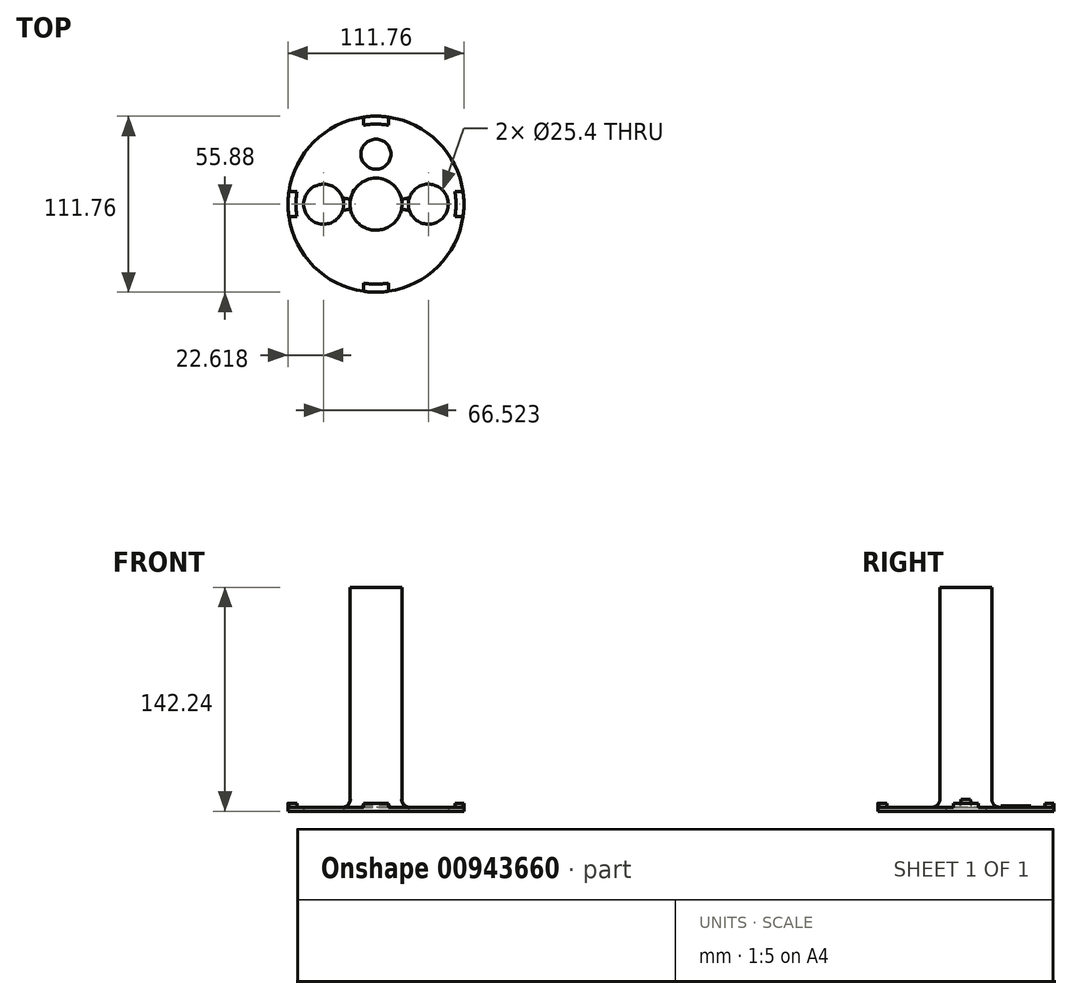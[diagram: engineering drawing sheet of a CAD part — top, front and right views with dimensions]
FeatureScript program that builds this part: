
annotation { "Feature Type Name" : "Feature", "Feature Type Description" : "" }
export const myFeature = defineFeature(function(context is Context, id is Id, definition is map)
    precondition{}
    {
        {
            var Q0;
            Q0=qCreatedBy(makeId("Top.planeOp"),FACE);
            var sketch = newSketch(context, id + "F0", { "sketchPlane" : qUnion([Q0])});
            skCircle(sketch, "E0", {"center": v(0, 0) * mm, "radius": 55.88 * mm});
            skCircle(sketch, "E1", {"center": v(0, 0) * mm, "radius": 16.51 * mm});
            skCircle(sketch, "E2", {"center": v(-33.26, 0) * mm, "radius": 12.7 * mm});
            skCircle(sketch, "E3.MirrorC", {"center": v(33.26, 0) * mm, "radius": 12.7 * mm});
            skCircle(sketch, "E4", {"center": v(0, 0) * mm, "radius": 50.8 * mm});
            skLineSegment(sketch, "E5", {"start": v(-50.18, 7.91) * mm, "end": v(-55.32, 7.91) * mm});
            skLineSegment(sketch, "E6.MirrorCS", {"start": v(-50.18, -7.91) * mm, "end": v(-55.32, -7.91) * mm});
            skLineSegment(sketch, "E7.1.0", {"start": v(-7.91, -50.18) * mm, "end": v(-7.91, -55.32) * mm});
            skLineSegment(sketch, "E7.1.1", {"start": v(7.91, -50.18) * mm, "end": v(7.91, -55.32) * mm});
            skLineSegment(sketch, "E7.2.0", {"start": v(50.18, -7.91) * mm, "end": v(55.32, -7.91) * mm});
            skLineSegment(sketch, "E7.2.1", {"start": v(50.18, 7.91) * mm, "end": v(55.32, 7.91) * mm});
            skLineSegment(sketch, "E7.3.0", {"start": v(7.91, 50.18) * mm, "end": v(7.91, 55.32) * mm});
            skLineSegment(sketch, "E7.3.1", {"start": v(-7.91, 50.18) * mm, "end": v(-7.91, 55.32) * mm});
            skSolve(sketch);
        }
        {
            var Q0;
            Q0 = qSketchRegion(id + "F0", true);
            var Q1;
            Q1=makeQuery(id+"F0.imprint","IMPRINT",FACE,{"disambiguationData":[TD([[makeQuery(id+"F0.imprint","IMPRINT",EDGE,{"derivedFrom":sQuery(id+"F0.wireOp",EDGE,"E1")}),-1.0]])]});
            var Q2;
            Q2=makeQuery(id+"F0.imprint","IMPRINT",FACE,{"disambiguationData":[TD([[makeQuery(id+"F0.imprint","IMPRINT",EDGE,{"derivedFrom":sQuery(id+"F0.wireOp",EDGE,"E1")}),1.0]])]});
            extrude(context, id + "F1", {"entities" : qUnion([Q0, Q1, Q2]), "depth" : 2.54 * mm, "offsetDistance" : 25.4 * mm});
        }
        {
            var Q0;
            {var subQ0=sQuery(id+"F0.wireOp",EDGE,"E5");Q0=makeQuery(id+"F0.imprint","IMPRINT",FACE,{"disambiguationData":[TD([[makeQuery(id+"F0.imprint","IMPRINT",EDGE,{"derivedFrom":subQ0}),1.0]])]});}
            var Q1;
            {var subQ0=sQuery(id+"F0.wireOp",EDGE,"E7.3.0");Q1=makeQuery(id+"F0.imprint","IMPRINT",FACE,{"disambiguationData":[TD([[makeQuery(id+"F0.imprint","IMPRINT",EDGE,{"derivedFrom":subQ0}),1.0]])]});}
            var Q2;
            {var subQ0=sQuery(id+"F0.wireOp",EDGE,"E7.2.0");Q2=makeQuery(id+"F0.imprint","IMPRINT",FACE,{"disambiguationData":[TD([[makeQuery(id+"F0.imprint","IMPRINT",EDGE,{"derivedFrom":subQ0}),1.0]])]});}
            var Q3;
            {var subQ0=sQuery(id+"F0.wireOp",EDGE,"E7.1.0");Q3=makeQuery(id+"F0.imprint","IMPRINT",FACE,{"disambiguationData":[TD([[makeQuery(id+"F0.imprint","IMPRINT",EDGE,{"derivedFrom":subQ0}),1.0]])]});}
            extrude(context, id + "F2", {"entities" : qUnion([Q0, Q1, Q2, Q3]), "operationType" : NewBodyOperationType.ADD, "depth" : 5.08 * mm, "offsetDistance" : 25.4 * mm});
        }
        {
            var Q0;
            Q0=makeQuery(id+"F0.imprint","IMPRINT",FACE,{"disambiguationData":[TD([[makeQuery(id+"F0.imprint","IMPRINT",EDGE,{"derivedFrom":sQuery(id+"F0.wireOp",EDGE,"E1")}),1.0]])]});
            extrude(context, id + "F3", {"entities" : qUnion([Q0]), "operationType" : NewBodyOperationType.ADD, "depth" : 142.24 * mm, "offsetDistance" : 25.4 * mm});
        }
        {
            var Q0;
            Q0=makeQuery(id+"F3.boolean.opBoolean","INTERSECT",EDGE,{"derivedFrom":[makeQuery(id+"F1.opExtrude","CAP_FACE",FACE,{"disambiguationData":[OSD([sQuery(id+"F0.wireOp",EDGE,"E0"),sQuery(id+"F0.wireOp",EDGE,"E2"),sQuery(id+"F0.wireOp",EDGE,"E3.MirrorC")])],"isStart":false}),makeQuery(id+"F3.opExtrude","SWEPT_FACE",FACE,{"disambiguationData":[OSD([sQuery(id+"F0.wireOp",EDGE,"E1")])]})]});
            fillet(context, id + "F4", {"entities" : qUnion([Q0]), "radius" : 5.08 * mm, "tangentPropagation" : true, "allowEdgeOverflow" : false});
        }
        {
            var Q0;
            Q0=makeQuery(id+"F1.opExtrude","CAP_FACE",FACE,{"disambiguationData":[OSD([sQuery(id+"F0.wireOp",EDGE,"E0"),sQuery(id+"F0.wireOp",EDGE,"E2"),sQuery(id+"F0.wireOp",EDGE,"E3.MirrorC")])],"isStart":false});
            var sketch = newSketch(context, id + "F5", { "sketchPlane" : qUnion([Q0])});
            skLineSegment(sketch, "E8", {"start": v(0, 0) * mm, "end": v(0, 31.75) * mm});
            skCircle(sketch, "E9", {"center": v(0, 31.75) * mm, "radius": 9.53 * mm});
            skSolve(sketch);
        }
        {
            var Q0;
            Q0 = qSketchRegion(id + "F5", true);
            extrude(context, id + "F6", {"entities" : qUnion([Q0]), "operationType" : NewBodyOperationType.ADD, "depth" : 0.76 * mm, "offsetDistance" : 25.4 * mm});
        }
    });
